# Revit family: NBS_wediSystems-UK-Ltd_ShwrTrys_wediFundoRiolitoneofloorelement
name_source: partatom
category: Plumbing Fixtures
units: mm (PartAtom-declared; Revit-internal decimal feet)

## family parameters
Cut with Voids When Loaded = No
Host = Face
Part Type = Normal
Room Calculation Point = No
Round Connector Dimension = Use Diameter
Shared = No

## types (11) — shared parameters
AccessibilityPerformance = Suitable for wheelchair users
Applications = Private housing, publicly accessible buildings and workplaces
AssetType = Fixed
Category = Pr_40_20_06_84:Shower trays
CodePerformance = EN 1606, EN 826, EN 13164, EN 13501
Default Elevation = 1219 mm
Description = Neo floor-level shower element with a channel drain
DurationUnit = year
ExpectedLife = 30
FaceFinish = <By Category>
Features = Fully watertight, close to wall drainage,extremely flat surface, suitable for wheelchair users
GlassMosaicSize = 20 x 20 mm
HasTray = Yes
IfcExportAs = IfcSanitaryTerminalType
IfcExportType = SHOWER
ManufacturerName = wedi Systems (UK) Ltd
ManufacturerURL = https://www.wedi.de
Material = A waterproof extruded polystyrene rigid foam core with a special, resistant and glass fibre reinforced cement coating
ModelReference = wedi Fundo Riolito neo floor element
NBSCertification = www.nationalbimlibrary.com/cert/3jjk5ao0
NBSDescription = Shower trays
NBSReference = 45-35-70/336
ProductInformation = https://www.wedi.de
Shape = Square
TileSize = 50 x 50 mm
Uniclass2015Code = Pr_40_20_06_84
Uniclass2015Title = Shower trays
Uniclass2015Version = Products v1.16
Version = 3
WarrantyDurationUnit = year
WasteHole = DN50
WediStructuralMaterial = NBS_wedi_PolystyreneExpanded
zero-valued in all types: DrainSize

## per-type parameters (varying)
| type | BIMObjectName | DrainWidth | Length | ModelNumber | Name | NominalHeight | NominalLength | NominalWidth | Size | Width |
| Fundo Riolito neo 900x900x50mm_800mmChannel | NBS_wediSystemsLtd_ShowerTrays_wediFundoRiolitoneofloorelement_900x900x50mm_800mmChannel | 800 mm | 900 mm  [stored 2.95276 ft] | 75100003 | ShowerTrays_wediFundoRiolitoneofloorelement_900x900x50mm_800mmChannel_wediSystemsLtd | 50 mm | 900 mm  [stored 2.95276 ft] | 900 mm  [stored 2.95276 ft] | 900 x 900 x 50 mm | 900 mm  [stored 2.95276 ft] |
| Fundo Riolito neo 1000x1000x50mm_800mmChannel | NBS_wediSystemsLtd_ShowerTrays_wediFundoRiolitoneofloorelement_1000x1000x50mm_800mmChannel | 800 mm | 1000 mm  [stored 3.28084 ft] | 75100032 | ShowerTrays_wediFundoRiolitoneofloorelement_1000x1000x50mm_800mmChannel_wediSystemsLtd | 50 mm | 1000 mm  [stored 3.28084 ft] | 1000 mm  [stored 3.28084 ft] | 1000 x 1000 x 50 mm | 1000 mm  [stored 3.28084 ft] |
| Fundo Riolito neo 1200x1200x50mm_1000mmChannel | NBS_wediSystemsLtd_ShowerTrays_wediFundoRiolitoneofloorelement_1200x1200x50mm_1000mmChannel | 1000 mm  [stored 3.28084 ft] | 1200 mm | 75100010 | ShowerTrays_wediFundoRiolitoneofloorelement_1200x1200x50mm_1000mmChannel_wediSystemsLtd | 50 mm | 1200 mm | 1200 mm | 1200 x 1200 x 50 mm | 1200 mm |
| Fundo Riolito neo 900x900x50mm_300mmChannel | NBS_wediSystemsLtd_ShowerTrays_wediFundoRiolitoneofloorelement_900x900x50mm_300mmChannel | 300 mm | 900 mm  [stored 2.95276 ft] | 75100031 | ShowerTrays_wediFundoRiolitoneofloorelement_900x900x50mm_300mmChannel_wediSystemsLtd | 50 mm | 900 mm  [stored 2.95276 ft] | 900 mm  [stored 2.95276 ft] | 900 x 900 x 50 mm | 900 mm  [stored 2.95276 ft] |
| Fundo Riolito neo 1200x900x50mm_700mmChannel | NBS_wediSystemsLtd_ShowerTrays_wediFundoRiolitoneofloorelement_1200x900x50mm_700mmChannel | 700 mm | 1200 mm | 75100001 | ShowerTrays_wediFundoRiolitoneofloorelement_1200x900x50mm_700mmChannel_wediSystemsLtd | 50 mm | 1200 mm | 900 mm  [stored 2.95276 ft] | 1200 x 900 x 50 mm | 900 mm  [stored 2.95276 ft] |
| Fundo Riolito neo 1400x900x50mm_700mmChannel | NBS_wediSystemsLtd_ShowerTrays_wediFundoRiolitoneofloorelement_1400x900x50mm_700mmChannel | 700 mm | 1400 mm | 75100033 | ShowerTrays_wediFundoRiolitoneofloorelement_1400x900x50mm_700mmChannel_wediSystemsLtd | 50 mm | 1400 mm | 900 mm  [stored 2.95276 ft] | 1200 x 900 x 50 mm | 900 mm  [stored 2.95276 ft] |
| Fundo Riolito neo 1200x900x50mm_800mmChannel | NBS_wediSystemsLtd_ShowerTrays_wediFundoRiolitoneofloorelement_1200x900x50mm_800mmChannel | 800 mm | 1200 mm | 75100034 | ShowerTrays_wediFundoRiolitoneofloorelement_1200x900x50mm_800mmChannel_wediSystemsLtd | 50 mm | 1200 mm | 900 mm  [stored 2.95276 ft] | 1600 x 1000 x 50 mm | 900 mm  [stored 2.95276 ft] |
| Fundo Riolito neo 1800x900x60mm_800mmChannel | NBS_wediSystemsLtd_ShowerTrays_wediFundoRiolitoneofloorelement_1800x900x60mm_800mmChannel | 800 mm | 1800 mm | 75100005 | ShowerTrays_wediFundoRiolitoneofloorelement_1800x900x60mm_800mmChannel_wediSystemsLtd | 60 mm  [stored 0.19685 ft] | 1800 mm | 900 mm  [stored 2.95276 ft] | 1800 x 900 x 60 mm | 900 mm  [stored 2.95276 ft] |
| Fundo Riolito neo 1200x1000x50mm_900mmChannel | NBS_wediSystemsLtd_ShowerTrays_wediFundoRiolitoneofloorelement_1200x1000x50mm_900mmChannel | 900 mm  [stored 2.95276 ft] | 1200 mm | 75100008 | ShowerTrays_wediFundoRiolitoneofloorelement_1200x1000x50mm_900mmChannel_wediSystemsLtd | 50 mm | 1200 mm | 1000 mm  [stored 3.28084 ft] | 1200 x 1000 x 50 mm | 1000 mm  [stored 3.28084 ft] |
| Fundo Riolito neo 1200x800x50mm_700mmChannel | NBS_wediSystemsLtd_ShowerTrays_wediFundoRiolitoneofloorelement_1200x800x50mm_700mmChannel | 700 mm | 1200 mm | 75100001 | ShowerTrays_wediFundoRiolitoneofloorelement_1200x800x50mm_700mmChannel_wediSystemsLtd | 50 mm | 1200 mm | 800 mm | 1200 x 800 x 50 mm | 800 mm |
| Fundo Riolito neo 1600x1000x50mm_800mmChannel | NBS_wediSystemsLtd_ShowerTrays_wediFundoRiolitoneofloorelement_1600x1000x50mm_800mmChannel | 800 mm | 1600 mm | 75100034 | ShowerTrays_wediFundoRiolitoneofloorelement_1600x1000x50mm_800mmChannel_wediSystemsLtd | 50 mm | 1600 mm | 1000 mm  [stored 3.28084 ft] | 1600 x 100 x 50 mm | 1000 mm  [stored 3.28084 ft] |

note: [stored X ft] marks values corroborated as IEEE doubles in the binary element streams (Revit-internal decimal feet)

## geometry (parser evidence)
native form markers: Sweep x2
no freeform markers — native parametric forms only
